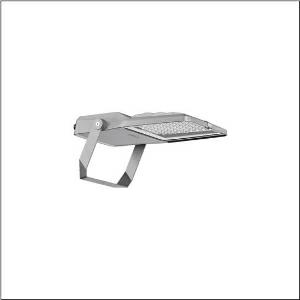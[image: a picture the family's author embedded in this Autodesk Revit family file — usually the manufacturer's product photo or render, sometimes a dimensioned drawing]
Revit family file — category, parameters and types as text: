
# Revit family: floodlight_fl_21_mini___pl52_5xa7776b4d1a_8ffb
name_source: partatom
category: Lighting Fixtures
units: mm (PartAtom-declared; Revit-internal decimal feet)

## family parameters
Cut with Voids When Loaded = No
Host = Face
Light Source = No
Part Type = Normal
Room Calculation Point = No
Round Connector Dimension = Use Diameter
Shared = No

## types (1)
- --- (1 x LED, 6480 lm, 45.7 W, 4000K)
    Apparent Load = 46 VA
    CIE Flux Codes = 26 60 98 100 100
    Color Rendering = 70
    Color Temperature = 4000K
    Default Elevation = 1800 mm
    Description = Floodlight FL 21 mini, floodlight, primary light control with lens, of PMMA, primary optical cover: protective disc, of toughened safety glass, transparent, light distribution: PL52, light emission: direct distribution, installation type: surface-mounted, LED, High Power LED, rated luminous flux: 6.480lm, luminous efficacy: 142lm/W, light colour: 740, colour temperature: 4000K, control gear: D4iSmart Interface (Zhaga), control: overheat protection, constant luminous flux control, time-dependent luminous flux control, flexible luminous flux parameterisation, pre-setting: logarithmic dimming characteristic, with terminal, 6-pole, mains connection: 220..240V, AC, 50/60Hz, start of lifetime: 46W, end of service life: 48W, reduction: 22W, mounting bracket, of diecast aluminium, powder-coated, SITECO metallic grey (DB 702S), corrosivity category C5 mid according to DIN EN ISO 12944, suitable for swimming pools, chlorine-resistant, sealing non-destructively replaceable, mounting bracket, of steel, galvanised, powder-coated, SITECO metallic grey (DB 702S), Smart Interface below and above, protection rating (complete): IP66, insulation class (complete): insulation class II (safety insulation), certification: CE, ENEC, VDE, protection symbol: D, impact resistance: IK08, permissible operating ambient temperature: -40..+40°C, permissible operating ambient temperature for outdoor applications: -40..+50°C, standard: DIN EN 12944, LABS conformity tested according to VDMA 24364:2018-05, packaging unit: 1 piece

Light Distribution: PL52
    Height = 70 mm
    Lamp = 1 x LED
    Lamp Light Flux = 6480 lm
    Lamp Power = 45.7 W
    Lamp count = 1
    Length = 485 mm
    Luminous efficacy = 142 lm/W
    Manufacturer = Siteco
    ModVariant = No
    Model = 5XA7776B4D1A
    Number of Poles = 1
    OnlyDefault = Yes
    Power Factor = 1
    Product Name = Floodlight FL 21 mini | PL52
    Product group = floodlight | pylon annexe
    ProductGroupID = 6201
    Protection Class = Protection class II
    Protection Degree = IP 66
    RLX_Detail_Level = 1
    RLX_Emergency_Light_Flux = 0 lm
    RLX_Emergency_Type = 0
    RLX_Emergency_Type_DB = No
    RlxData = <blob elided: 96229 chars, md5=b7391863>
    Socket = socket
    Standby Power = 0 W
    System Light Flux = 6480 lm
    System Power = 46 W
    Type Comments = factory setting: luminous flux: 100 % | dim-lin: 254 | 463 mA
    Type Image = l_1006845.jpg
    URL = http://relux.com
    VarID = @adj_099405
    Voltage = 0 V
    Weight = 0.00 kg
    Width = 337 mm

## geometry (parser evidence)
native form markers: Blend x4, Sweep x13
no freeform markers — native parametric forms only
